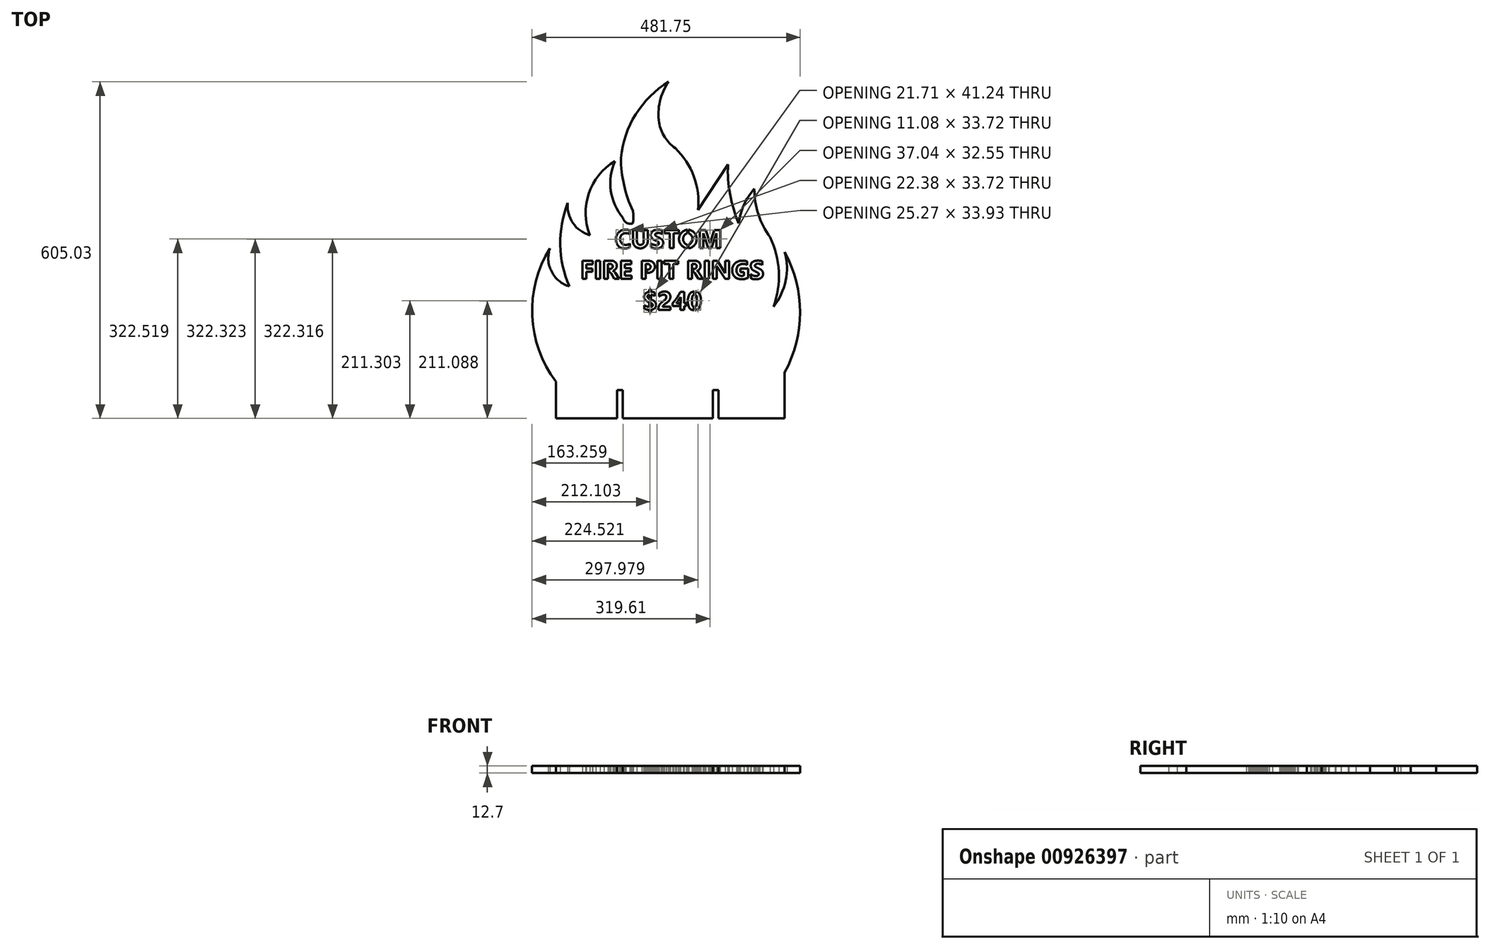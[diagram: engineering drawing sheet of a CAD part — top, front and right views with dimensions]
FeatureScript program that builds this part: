
annotation { "Feature Type Name" : "Feature", "Feature Type Description" : "" }
export const myFeature = defineFeature(function(context is Context, id is Id, definition is map)
    precondition{}
    {
        {
            var Q0;
            Q0=qCreatedBy(makeId("Top.planeOp"),FACE);
            var sketch = newSketch(context, id + "F0", { "sketchPlane" : qUnion([Q0])});
            skArc(sketch, "E0", {"start": v(108.84, 331.84) * mm, "mid": v(102.03, 332.98) * mm, "end": v(95.2, 331.92) * mm});
            skArc(sketch, "E1", {"start": v(95.2, 331.92) * mm, "mid": v(85.87, 324.34) * mm, "end": v(84.03, 312.45) * mm});
            skArc(sketch, "E2", {"start": v(84.03, 312.45) * mm, "mid": v(89.83, 302.02) * mm, "end": v(101.45, 299.3) * mm});
            skArc(sketch, "E3", {"start": v(101.45, 299.3) * mm, "mid": v(105.29, 299.76) * mm, "end": v(108.84, 301.28) * mm});
            skArc(sketch, "E4", {"start": v(96.85, 306.45) * mm, "mid": v(103.08, 305.63) * mm, "end": v(108.92, 307.93) * mm});
            skArc(sketch, "E5", {"start": v(91.34, 317.62) * mm, "mid": v(92.31, 311.16) * mm, "end": v(96.85, 306.45) * mm});
            skArc(sketch, "E6", {"start": v(98.74, 326.41) * mm, "mid": v(93.7, 323.14) * mm, "end": v(91.34, 317.62) * mm});
            skArc(sketch, "E7", {"start": v(108.84, 324.52) * mm, "mid": v(103.99, 326.53) * mm, "end": v(98.74, 326.41) * mm});
            skLineSegment(sketch, "E8", {"start": v(108.84, 331.84) * mm, "end": v(108.84, 324.52) * mm});
            skLineSegment(sketch, "E9", {"start": v(108.92, 307.93) * mm, "end": v(108.84, 301.28) * mm});
            skLineSegment(sketch, "E10", {"start": v(114.18, 332.5) * mm, "end": v(121.57, 332.5) * mm});
            skLineSegment(sketch, "E11", {"start": v(121.57, 332.5) * mm, "end": v(121.57, 311.55) * mm});
            skLineSegment(sketch, "E12", {"start": v(114.18, 332.5) * mm, "end": v(114.18, 311.22) * mm});
            skLineSegment(sketch, "E13", {"start": v(133.65, 332.5) * mm, "end": v(141.12, 332.5) * mm});
            skLineSegment(sketch, "E14", {"start": v(141.12, 332.5) * mm, "end": v(141.12, 311.63) * mm});
            skLineSegment(sketch, "E15", {"start": v(133.65, 332.5) * mm, "end": v(133.65, 311.63) * mm});
            skArc(sketch, "E16", {"start": v(121.57, 311.55) * mm, "mid": v(127.65, 305.59) * mm, "end": v(133.65, 311.63) * mm});
            skArc(sketch, "E17", {"start": v(114.18, 311.22) * mm, "mid": v(127.84, 299.32) * mm, "end": v(141.12, 311.63) * mm});
            skArc(sketch, "E18", {"start": v(167.33, 325.02) * mm, "mid": v(162.06, 326.88) * mm, "end": v(156.49, 326.41) * mm});
            skArc(sketch, "E19", {"start": v(156.49, 326.41) * mm, "mid": v(154.37, 324.68) * mm, "end": v(155.17, 322.06) * mm});
            skArc(sketch, "E20", {"start": v(155.17, 322.06) * mm, "mid": v(156.94, 320.64) * mm, "end": v(158.95, 319.6) * mm});
            skArc(sketch, "E21", {"start": v(166.43, 315.24) * mm, "mid": v(162.87, 317.73) * mm, "end": v(158.95, 319.6) * mm});
            skArc(sketch, "E22", {"start": v(168.07, 305.22) * mm, "mid": v(168.61, 310.45) * mm, "end": v(166.43, 315.24) * mm});
            skArc(sketch, "E23", {"start": v(159.77, 299.47) * mm, "mid": v(164.61, 301.34) * mm, "end": v(168.07, 305.22) * mm});
            skArc(sketch, "E24", {"start": v(146.63, 301.28) * mm, "mid": v(153.06, 299.37) * mm, "end": v(159.77, 299.47) * mm});
            skArc(sketch, "E25", {"start": v(146.55, 308.34) * mm, "mid": v(149.66, 306.42) * mm, "end": v(153.2, 305.47) * mm});
            skArc(sketch, "E26", {"start": v(153.2, 305.47) * mm, "mid": v(156.77, 305.1) * mm, "end": v(160.1, 306.45) * mm});
            skArc(sketch, "E27", {"start": v(160.1, 306.45) * mm, "mid": v(160.96, 308.28) * mm, "end": v(160.47, 310.23) * mm});
            skArc(sketch, "E28", {"start": v(160.47, 310.23) * mm, "mid": v(158.3, 312.04) * mm, "end": v(155.7, 313.15) * mm});
            skArc(sketch, "E29", {"start": v(148.35, 317.75) * mm, "mid": v(151.7, 314.9) * mm, "end": v(155.7, 313.15) * mm});
            skArc(sketch, "E30", {"start": v(146.83, 326.13) * mm, "mid": v(146.5, 321.74) * mm, "end": v(148.35, 317.75) * mm});
            skArc(sketch, "E31", {"start": v(154.6, 332.37) * mm, "mid": v(149.89, 330.28) * mm, "end": v(146.83, 326.13) * mm});
            skArc(sketch, "E32", {"start": v(167.17, 331.67) * mm, "mid": v(160.93, 332.85) * mm, "end": v(154.6, 332.37) * mm});
            skLineSegment(sketch, "E33", {"start": v(167.17, 331.67) * mm, "end": v(167.33, 325.02) * mm});
            skLineSegment(sketch, "E34", {"start": v(146.63, 301.28) * mm, "end": v(146.55, 308.34) * mm});
            skLineSegment(sketch, "E35", {"start": v(171.08, 332.5) * mm, "end": v(196.87, 332.5) * mm});
            skLineSegment(sketch, "E36", {"start": v(196.87, 332.5) * mm, "end": v(196.87, 326.44) * mm});
            skLineSegment(sketch, "E37", {"start": v(196.87, 326.44) * mm, "end": v(187.54, 326.44) * mm});
            skLineSegment(sketch, "E38", {"start": v(187.54, 326.44) * mm, "end": v(187.54, 299.95) * mm});
            skLineSegment(sketch, "E39", {"start": v(187.54, 299.95) * mm, "end": v(180.38, 299.95) * mm});
            skLineSegment(sketch, "E40", {"start": v(180.38, 299.95) * mm, "end": v(180.38, 326.44) * mm});
            skLineSegment(sketch, "E41", {"start": v(180.38, 326.44) * mm, "end": v(171.08, 326.44) * mm});
            skLineSegment(sketch, "E42", {"start": v(171.08, 326.44) * mm, "end": v(171.08, 332.5) * mm});
            skLineSegment(sketch, "E43", {"start": v(234.12, 332.5) * mm, "end": v(244.97, 332.5) * mm});
            skLineSegment(sketch, "E44", {"start": v(244.97, 332.5) * mm, "end": v(252.7, 308.44) * mm});
            skLineSegment(sketch, "E45", {"start": v(234.12, 332.5) * mm, "end": v(234.12, 299.95) * mm});
            skLineSegment(sketch, "E46", {"start": v(234.12, 299.95) * mm, "end": v(240.8, 299.95) * mm});
            skLineSegment(sketch, "E47", {"start": v(240.8, 299.95) * mm, "end": v(240.5, 326.23) * mm});
            skLineSegment(sketch, "E48", {"start": v(240.5, 326.23) * mm, "end": v(249.5, 299.95) * mm});
            skLineSegment(sketch, "E49", {"start": v(249.5, 299.95) * mm, "end": v(255.46, 299.95) * mm});
            skLineSegment(sketch, "E50", {"start": v(255.46, 299.95) * mm, "end": v(264.18, 326.2) * mm});
            skLineSegment(sketch, "E51", {"start": v(264.18, 326.2) * mm, "end": v(264.18, 299.95) * mm});
            skLineSegment(sketch, "E52", {"start": v(264.18, 299.95) * mm, "end": v(271.16, 299.95) * mm});
            skLineSegment(sketch, "E53", {"start": v(271.16, 299.95) * mm, "end": v(271.16, 332.5) * mm});
            skLineSegment(sketch, "E54", {"start": v(271.16, 332.5) * mm, "end": v(260.73, 332.44) * mm});
            skLineSegment(sketch, "E55", {"start": v(260.73, 332.44) * mm, "end": v(252.7, 308.44) * mm});
            skLineSegment(sketch, "E56", {"start": v(212.35, 305.64) * mm, "end": v(212.35, 299.43) * mm});
            skLineSegment(sketch, "E57", {"start": v(214.07, 299.34) * mm, "end": v(214.07, 305.67) * mm});
            skLineSegment(sketch, "E58", {"start": v(212.24, 332.8) * mm, "end": v(212.24, 326.62) * mm});
            skLineSegment(sketch, "E59", {"start": v(213.94, 326.58) * mm, "end": v(213.94, 332.78) * mm});
            skArc(sketch, "E60", {"start": v(212.24, 332.8) * mm, "mid": v(197.08, 316.07) * mm, "end": v(212.35, 299.43) * mm});
            skArc(sketch, "E61", {"start": v(214.07, 299.34) * mm, "mid": v(228.95, 316.12) * mm, "end": v(213.94, 332.78) * mm});
            skArc(sketch, "E62", {"start": v(212.24, 326.62) * mm, "mid": v(204.51, 316.1) * mm, "end": v(212.35, 305.64) * mm});
            skArc(sketch, "E63", {"start": v(214.07, 305.67) * mm, "mid": v(221.3, 316.17) * mm, "end": v(213.94, 326.58) * mm});
            skLineSegment(sketch, "E64", {"start": v(23.38, 277.03) * mm, "end": v(42.19, 277.03) * mm});
            skLineSegment(sketch, "E65", {"start": v(42.19, 277.03) * mm, "end": v(42.19, 270.93) * mm});
            skLineSegment(sketch, "E66", {"start": v(42.19, 270.93) * mm, "end": v(30.72, 270.93) * mm});
            skLineSegment(sketch, "E67", {"start": v(30.72, 270.93) * mm, "end": v(30.72, 262.92) * mm});
            skLineSegment(sketch, "E68", {"start": v(30.72, 262.92) * mm, "end": v(41.2, 262.92) * mm});
            skLineSegment(sketch, "E69", {"start": v(41.2, 262.92) * mm, "end": v(41.2, 257.13) * mm});
            skLineSegment(sketch, "E70", {"start": v(41.2, 257.13) * mm, "end": v(30.74, 257.13) * mm});
            skLineSegment(sketch, "E71", {"start": v(30.74, 257.13) * mm, "end": v(30.74, 244.43) * mm});
            skLineSegment(sketch, "E72", {"start": v(30.74, 244.43) * mm, "end": v(23.38, 244.43) * mm});
            skLineSegment(sketch, "E73", {"start": v(23.38, 244.43) * mm, "end": v(23.38, 277.03) * mm});
            skLineSegment(sketch, "E74.bottom", {"start": v(47.55, 277.03) * mm, "end": v(55.04, 277.03) * mm});
            skLineSegment(sketch, "E74.top", {"start": v(47.55, 244.43) * mm, "end": v(55.04, 244.43) * mm});
            skLineSegment(sketch, "E74.left", {"start": v(47.55, 277.03) * mm, "end": v(47.55, 244.43) * mm});
            skLineSegment(sketch, "E74.right", {"start": v(55.04, 277.03) * mm, "end": v(55.04, 244.43) * mm});
            skLineSegment(sketch, "E75", {"start": v(62.3, 244.43) * mm, "end": v(62.3, 277.03) * mm});
            skLineSegment(sketch, "E76", {"start": v(62.3, 277.03) * mm, "end": v(76.13, 277.03) * mm});
            skLineSegment(sketch, "E77", {"start": v(62.3, 244.43) * mm, "end": v(69.5, 244.43) * mm});
            skLineSegment(sketch, "E78", {"start": v(69.5, 244.43) * mm, "end": v(69.5, 271.2) * mm});
            skLineSegment(sketch, "E79", {"start": v(69.5, 271.2) * mm, "end": v(74.39, 271.2) * mm});
            skLineSegment(sketch, "E80", {"start": v(71.2, 262.43) * mm, "end": v(73.51, 262.43) * mm});
            skLineSegment(sketch, "E81", {"start": v(71.2, 262.43) * mm, "end": v(71.2, 256.8) * mm});
            skLineSegment(sketch, "E82", {"start": v(71.2, 256.8) * mm, "end": v(71.77, 256.8) * mm});
            skLineSegment(sketch, "E83", {"start": v(74.9, 254.53) * mm, "end": v(80.9, 244.43) * mm});
            skLineSegment(sketch, "E84", {"start": v(80.9, 244.43) * mm, "end": v(89.31, 244.43) * mm});
            skLineSegment(sketch, "E85", {"start": v(89.31, 244.43) * mm, "end": v(82.46, 255.51) * mm});
            skArc(sketch, "E86", {"start": v(73.51, 262.43) * mm, "mid": v(77.92, 266.42) * mm, "end": v(74.39, 271.2) * mm});
            skArc(sketch, "E87", {"start": v(74.9, 254.53) * mm, "mid": v(73.58, 255.98) * mm, "end": v(71.77, 256.8) * mm});
            skArc(sketch, "E88", {"start": v(82.46, 255.51) * mm, "mid": v(80.72, 257.54) * mm, "end": v(78.44, 258.93) * mm});
            skArc(sketch, "E89", {"start": v(78.44, 258.93) * mm, "mid": v(85.25, 269) * mm, "end": v(76.13, 277.03) * mm});
            skLineSegment(sketch, "E90", {"start": v(92.56, 244.46) * mm, "end": v(92.56, 276.9) * mm});
            skLineSegment(sketch, "E91", {"start": v(92.56, 276.9) * mm, "end": v(111.32, 276.9) * mm});
            skLineSegment(sketch, "E92", {"start": v(111.32, 276.9) * mm, "end": v(111.32, 270.93) * mm});
            skLineSegment(sketch, "E93", {"start": v(111.32, 270.93) * mm, "end": v(99.9, 270.93) * mm});
            skLineSegment(sketch, "E94", {"start": v(99.9, 270.93) * mm, "end": v(99.9, 263.66) * mm});
            skLineSegment(sketch, "E95", {"start": v(99.9, 263.66) * mm, "end": v(110.4, 263.66) * mm});
            skLineSegment(sketch, "E96", {"start": v(110.4, 263.66) * mm, "end": v(110.4, 257.75) * mm});
            skLineSegment(sketch, "E97", {"start": v(110.4, 257.75) * mm, "end": v(99.9, 257.75) * mm});
            skLineSegment(sketch, "E98", {"start": v(99.9, 257.75) * mm, "end": v(99.9, 250.42) * mm});
            skLineSegment(sketch, "E99", {"start": v(99.9, 250.42) * mm, "end": v(111.86, 250.42) * mm});
            skLineSegment(sketch, "E100", {"start": v(111.86, 250.42) * mm, "end": v(111.86, 244.36) * mm});
            skLineSegment(sketch, "E101", {"start": v(111.86, 244.36) * mm, "end": v(92.56, 244.46) * mm});
            skLineSegment(sketch, "E102", {"start": v(130.03, 244.46) * mm, "end": v(130.03, 276.82) * mm});
            skLineSegment(sketch, "E103", {"start": v(130.03, 276.82) * mm, "end": v(143.4, 276.82) * mm});
            skLineSegment(sketch, "E104", {"start": v(130.03, 244.46) * mm, "end": v(137.35, 244.46) * mm});
            skLineSegment(sketch, "E105", {"start": v(137.35, 244.46) * mm, "end": v(137.35, 271.2) * mm});
            skLineSegment(sketch, "E106", {"start": v(137.35, 271.2) * mm, "end": v(141.55, 271.2) * mm});
            skLineSegment(sketch, "E107", {"start": v(138.92, 255.57) * mm, "end": v(138.92, 261.1) * mm});
            skLineSegment(sketch, "E108", {"start": v(138.92, 261.1) * mm, "end": v(140.87, 261.1) * mm});
            skArc(sketch, "E109", {"start": v(140.87, 261.1) * mm, "mid": v(145.94, 265.83) * mm, "end": v(141.55, 271.2) * mm});
            skArc(sketch, "E110", {"start": v(153.42, 264.02) * mm, "mid": v(151.53, 272.86) * mm, "end": v(143.4, 276.82) * mm});
            skArc(sketch, "E111", {"start": v(138.92, 255.57) * mm, "mid": v(147.84, 256.93) * mm, "end": v(153.42, 264.02) * mm});
            skLineSegment(sketch, "E112.bottom", {"start": v(158.46, 276.94) * mm, "end": v(165.74, 276.94) * mm});
            skLineSegment(sketch, "E112.top", {"start": v(158.46, 244.46) * mm, "end": v(165.74, 244.46) * mm});
            skLineSegment(sketch, "E112.left", {"start": v(158.46, 276.94) * mm, "end": v(158.46, 244.46) * mm});
            skLineSegment(sketch, "E112.right", {"start": v(165.74, 276.94) * mm, "end": v(165.74, 244.46) * mm});
            skLineSegment(sketch, "E113", {"start": v(170.03, 271) * mm, "end": v(170.03, 276.94) * mm});
            skLineSegment(sketch, "E114", {"start": v(170.03, 276.94) * mm, "end": v(195.82, 276.94) * mm});
            skLineSegment(sketch, "E115", {"start": v(195.82, 276.94) * mm, "end": v(195.82, 271.08) * mm});
            skLineSegment(sketch, "E116", {"start": v(195.82, 271.08) * mm, "end": v(186.62, 271.08) * mm});
            skLineSegment(sketch, "E117", {"start": v(186.62, 271.08) * mm, "end": v(186.62, 244.63) * mm});
            skLineSegment(sketch, "E118", {"start": v(186.62, 244.63) * mm, "end": v(179.48, 244.63) * mm});
            skLineSegment(sketch, "E119", {"start": v(179.48, 244.63) * mm, "end": v(179.48, 271.08) * mm});
            skLineSegment(sketch, "E120", {"start": v(179.48, 271.08) * mm, "end": v(170.03, 271) * mm});
            skLineSegment(sketch, "E121", {"start": v(213.11, 244.5) * mm, "end": v(213.11, 276.94) * mm});
            skLineSegment(sketch, "E122", {"start": v(213.11, 276.94) * mm, "end": v(226.58, 276.94) * mm});
            skLineSegment(sketch, "E123", {"start": v(213.11, 244.5) * mm, "end": v(220.5, 244.5) * mm});
            skLineSegment(sketch, "E124", {"start": v(220.5, 244.5) * mm, "end": v(220.5, 271.44) * mm});
            skLineSegment(sketch, "E125", {"start": v(220.5, 271.44) * mm, "end": v(224.92, 271.44) * mm});
            skLineSegment(sketch, "E126", {"start": v(222.09, 262.42) * mm, "end": v(222.09, 256.9) * mm});
            skLineSegment(sketch, "E127", {"start": v(222.09, 256.9) * mm, "end": v(222.93, 256.9) * mm});
            skLineSegment(sketch, "E128", {"start": v(222.09, 262.42) * mm, "end": v(224.2, 262.42) * mm});
            skLineSegment(sketch, "E129", {"start": v(225.52, 254.75) * mm, "end": v(231.88, 244.5) * mm});
            skLineSegment(sketch, "E130", {"start": v(231.88, 244.5) * mm, "end": v(240.27, 244.5) * mm});
            skLineSegment(sketch, "E131", {"start": v(240.27, 244.5) * mm, "end": v(232.78, 256.12) * mm});
            skArc(sketch, "E132", {"start": v(225.52, 254.75) * mm, "mid": v(224.48, 256) * mm, "end": v(223.13, 256.9) * mm});
            skArc(sketch, "E133", {"start": v(232.78, 256.12) * mm, "mid": v(231.29, 257.76) * mm, "end": v(229.35, 258.85) * mm});
            skArc(sketch, "E134", {"start": v(229.35, 258.85) * mm, "mid": v(235.73, 269.08) * mm, "end": v(226.58, 276.94) * mm});
            skArc(sketch, "E135", {"start": v(224.2, 262.42) * mm, "mid": v(228.73, 266.6) * mm, "end": v(224.92, 271.44) * mm});
            skLineSegment(sketch, "E136.bottom", {"start": v(243.31, 276.94) * mm, "end": v(250.8, 276.94) * mm});
            skLineSegment(sketch, "E136.top", {"start": v(243.31, 244.42) * mm, "end": v(250.8, 244.42) * mm});
            skLineSegment(sketch, "E136.left", {"start": v(243.31, 276.94) * mm, "end": v(243.31, 244.42) * mm});
            skLineSegment(sketch, "E136.right", {"start": v(250.8, 276.94) * mm, "end": v(250.8, 244.42) * mm});
            skLineSegment(sketch, "E137", {"start": v(258.1, 244.42) * mm, "end": v(258.1, 276.94) * mm});
            skLineSegment(sketch, "E138", {"start": v(258.1, 276.94) * mm, "end": v(265.96, 276.94) * mm});
            skLineSegment(sketch, "E139", {"start": v(265.96, 276.94) * mm, "end": v(280.37, 254.52) * mm});
            skLineSegment(sketch, "E140", {"start": v(280.37, 254.52) * mm, "end": v(280.37, 276.94) * mm});
            skLineSegment(sketch, "E141", {"start": v(280.37, 276.94) * mm, "end": v(287.16, 276.94) * mm});
            skLineSegment(sketch, "E142", {"start": v(287.16, 276.94) * mm, "end": v(287.21, 244.46) * mm});
            skLineSegment(sketch, "E143", {"start": v(287.21, 244.46) * mm, "end": v(279.88, 244.36) * mm});
            skLineSegment(sketch, "E144", {"start": v(279.88, 244.36) * mm, "end": v(264.84, 267.42) * mm});
            skLineSegment(sketch, "E145", {"start": v(264.84, 267.42) * mm, "end": v(264.84, 244.42) * mm});
            skLineSegment(sketch, "E146", {"start": v(264.84, 244.42) * mm, "end": v(258.1, 244.42) * mm});
            skLineSegment(sketch, "E147", {"start": v(319.74, 275.95) * mm, "end": v(319.74, 269.15) * mm});
            skLineSegment(sketch, "E148", {"start": v(314, 250.8) * mm, "end": v(314, 256.96) * mm});
            skLineSegment(sketch, "E149", {"start": v(314, 256.96) * mm, "end": v(307.43, 256.96) * mm});
            skLineSegment(sketch, "E150", {"start": v(307.43, 256.96) * mm, "end": v(307.43, 262.88) * mm});
            skLineSegment(sketch, "E151", {"start": v(307.43, 262.88) * mm, "end": v(321.25, 262.88) * mm});
            skLineSegment(sketch, "E152", {"start": v(321.25, 262.88) * mm, "end": v(321.25, 246.67) * mm});
            skArc(sketch, "E153", {"start": v(319.74, 269.15) * mm, "mid": v(311.3, 271.47) * mm, "end": v(303.19, 268.17) * mm});
            skArc(sketch, "E154", {"start": v(303.19, 268.17) * mm, "mid": v(300.3, 260.38) * mm, "end": v(303.19, 252.6) * mm});
            skArc(sketch, "E155", {"start": v(303.19, 252.6) * mm, "mid": v(308.3, 249.93) * mm, "end": v(314, 250.8) * mm});
            skArc(sketch, "E156", {"start": v(319.74, 275.95) * mm, "mid": v(310.68, 277.26) * mm, "end": v(301.74, 275.31) * mm});
            skArc(sketch, "E157", {"start": v(301.74, 275.31) * mm, "mid": v(294.33, 267.76) * mm, "end": v(292.79, 257.3) * mm});
            skArc(sketch, "E158", {"start": v(292.79, 257.3) * mm, "mid": v(296.71, 248.76) * mm, "end": v(304.99, 244.3) * mm});
            skArc(sketch, "E159", {"start": v(304.99, 244.3) * mm, "mid": v(313.34, 243.96) * mm, "end": v(321.25, 246.67) * mm});
            skArc(sketch, "E160", {"start": v(326.05, 252.95) * mm, "mid": v(330.49, 250.43) * mm, "end": v(335.54, 249.7) * mm});
            skArc(sketch, "E161", {"start": v(335.54, 249.7) * mm, "mid": v(338.07, 250) * mm, "end": v(340.07, 251.57) * mm});
            skArc(sketch, "E162", {"start": v(340.07, 251.57) * mm, "mid": v(340.28, 253.95) * mm, "end": v(338.62, 255.68) * mm});
            skArc(sketch, "E163", {"start": v(331.3, 259.44) * mm, "mid": v(334.93, 257.5) * mm, "end": v(338.62, 255.68) * mm});
            skArc(sketch, "E164", {"start": v(326.15, 266.04) * mm, "mid": v(327.94, 262.13) * mm, "end": v(331.3, 259.44) * mm});
            skArc(sketch, "E165", {"start": v(331.95, 276.26) * mm, "mid": v(327.09, 272.27) * mm, "end": v(326.15, 266.04) * mm});
            skArc(sketch, "E166", {"start": v(346.74, 276.26) * mm, "mid": v(339.34, 277.34) * mm, "end": v(331.95, 276.26) * mm});
            skArc(sketch, "E167", {"start": v(346.8, 269.43) * mm, "mid": v(342.9, 271.2) * mm, "end": v(338.62, 271.53) * mm});
            skArc(sketch, "E168", {"start": v(338.62, 271.53) * mm, "mid": v(336.04, 271.19) * mm, "end": v(334.02, 269.53) * mm});
            skArc(sketch, "E169", {"start": v(334.02, 269.53) * mm, "mid": v(333.75, 267.57) * mm, "end": v(335, 266.04) * mm});
            skArc(sketch, "E170", {"start": v(335, 266.04) * mm, "mid": v(338.47, 264.04) * mm, "end": v(342.1, 262.35) * mm});
            skArc(sketch, "E171", {"start": v(347.88, 256.2) * mm, "mid": v(345.68, 259.92) * mm, "end": v(342.1, 262.35) * mm});
            skArc(sketch, "E172", {"start": v(346.77, 248.22) * mm, "mid": v(348.04, 252.1) * mm, "end": v(347.88, 256.2) * mm});
            skArc(sketch, "E173", {"start": v(339.32, 244) * mm, "mid": v(343.39, 245.51) * mm, "end": v(346.77, 248.22) * mm});
            skArc(sketch, "E174", {"start": v(326.15, 245.56) * mm, "mid": v(328.4, 244.63) * mm, "end": v(330.76, 244.05) * mm});
            skLineSegment(sketch, "E175", {"start": v(326.05, 252.95) * mm, "end": v(326.15, 245.56) * mm});
            skLineSegment(sketch, "E176", {"start": v(346.74, 276.26) * mm, "end": v(346.8, 269.43) * mm});
            skArc(sketch, "E177", {"start": v(330.76, 244.05) * mm, "mid": v(335.04, 243.7) * mm, "end": v(339.32, 244) * mm});
            skLineSegment(sketch, "E178", {"start": v(143.42, 225.4) * mm, "end": v(146.63, 225.4) * mm});
            skLineSegment(sketch, "E179", {"start": v(146.63, 225.4) * mm, "end": v(146.63, 221.26) * mm});
            skLineSegment(sketch, "E180", {"start": v(143.42, 225.4) * mm, "end": v(143.42, 221.23) * mm});
            skLineSegment(sketch, "E181", {"start": v(143.39, 215.84) * mm, "end": v(143.39, 210.14) * mm});
            skLineSegment(sketch, "E182", {"start": v(143.39, 210.14) * mm, "end": v(146.67, 208.76) * mm});
            skLineSegment(sketch, "E183", {"start": v(146.67, 208.76) * mm, "end": v(146.67, 215.9) * mm});
            skArc(sketch, "E184", {"start": v(153.75, 219.74) * mm, "mid": v(150.29, 220.94) * mm, "end": v(146.63, 221.26) * mm});
            skArc(sketch, "E185", {"start": v(153.75, 213.7) * mm, "mid": v(150.33, 215.18) * mm, "end": v(146.67, 215.9) * mm});
            skArc(sketch, "E186", {"start": v(143.42, 221.23) * mm, "mid": v(138.89, 219.79) * mm, "end": v(135.48, 216.46) * mm});
            skArc(sketch, "E187", {"start": v(135.48, 216.46) * mm, "mid": v(134.34, 211.01) * mm, "end": v(136.82, 206.03) * mm});
            skArc(sketch, "E188", {"start": v(143.39, 215.84) * mm, "mid": v(140.98, 214.73) * mm, "end": v(140.38, 212.14) * mm});
            skArc(sketch, "E189", {"start": v(140.38, 212.14) * mm, "mid": v(141.48, 210.02) * mm, "end": v(143.42, 208.62) * mm});
            skArc(sketch, "E190", {"start": v(155.93, 198.47) * mm, "mid": v(154.07, 203.14) * mm, "end": v(149.98, 206.07) * mm});
            skArc(sketch, "E191", {"start": v(152.2, 190.7) * mm, "mid": v(155.21, 194.03) * mm, "end": v(155.93, 198.47) * mm});
            skArc(sketch, "E192", {"start": v(146.67, 188.9) * mm, "mid": v(149.55, 189.42) * mm, "end": v(152.2, 190.7) * mm});
            skArc(sketch, "E193", {"start": v(146.67, 194.22) * mm, "mid": v(148.96, 195.05) * mm, "end": v(149.92, 197.3) * mm});
            skArc(sketch, "E194", {"start": v(149.92, 197.3) * mm, "mid": v(148.94, 199.47) * mm, "end": v(147.01, 200.89) * mm});
            skArc(sketch, "E195", {"start": v(136.82, 206.03) * mm, "mid": v(139.24, 204.31) * mm, "end": v(141.9, 203.03) * mm});
            skLineSegment(sketch, "E196", {"start": v(143.42, 208.62) * mm, "end": v(149.98, 206.07) * mm});
            skLineSegment(sketch, "E197", {"start": v(147.01, 200.89) * mm, "end": v(141.9, 203.03) * mm});
            skLineSegment(sketch, "E198", {"start": v(146.67, 194.22) * mm, "end": v(146.67, 199.64) * mm});
            skLineSegment(sketch, "E199", {"start": v(146.67, 199.64) * mm, "end": v(143.42, 201) * mm});
            skLineSegment(sketch, "E200", {"start": v(143.42, 201) * mm, "end": v(143.42, 194.08) * mm});
            skArc(sketch, "E201", {"start": v(134.9, 197.09) * mm, "mid": v(138.95, 194.99) * mm, "end": v(143.42, 194.08) * mm});
            skLineSegment(sketch, "E202", {"start": v(134.9, 197.09) * mm, "end": v(134.9, 190.82) * mm});
            skArc(sketch, "E203", {"start": v(134.9, 190.82) * mm, "mid": v(139.02, 189.26) * mm, "end": v(143.4, 188.81) * mm});
            skLineSegment(sketch, "E204", {"start": v(143.4, 188.81) * mm, "end": v(143.4, 184.17) * mm});
            skLineSegment(sketch, "E205", {"start": v(143.4, 184.17) * mm, "end": v(146.67, 184.17) * mm});
            skLineSegment(sketch, "E206", {"start": v(146.67, 184.17) * mm, "end": v(146.67, 188.9) * mm});
            skLineSegment(sketch, "E207", {"start": v(153.75, 219.74) * mm, "end": v(153.75, 213.7) * mm});
            skLineSegment(sketch, "E208", {"start": v(161.6, 212.73) * mm, "end": v(161.6, 218.93) * mm});
            skArc(sketch, "E209", {"start": v(174.38, 221.48) * mm, "mid": v(167.76, 221.38) * mm, "end": v(161.6, 218.93) * mm});
            skArc(sketch, "E210", {"start": v(181.45, 214.13) * mm, "mid": v(179.03, 218.88) * mm, "end": v(174.38, 221.48) * mm});
            skArc(sketch, "E211", {"start": v(177.83, 203.82) * mm, "mid": v(180.88, 208.54) * mm, "end": v(181.45, 214.13) * mm});
            skArc(sketch, "E212", {"start": v(177.83, 203.82) * mm, "mid": v(173.98, 200.9) * mm, "end": v(170.15, 197.94) * mm});
            skArc(sketch, "E213", {"start": v(170.15, 197.94) * mm, "mid": v(168.78, 196.5) * mm, "end": v(167.93, 194.7) * mm});
            skLineSegment(sketch, "E214", {"start": v(167.93, 194.7) * mm, "end": v(181.53, 194.7) * mm});
            skLineSegment(sketch, "E215", {"start": v(181.53, 194.7) * mm, "end": v(181.53, 188.83) * mm});
            skLineSegment(sketch, "E216", {"start": v(181.53, 188.83) * mm, "end": v(160.09, 188.83) * mm});
            skLineSegment(sketch, "E217", {"start": v(160.09, 188.83) * mm, "end": v(160.09, 192.69) * mm});
            skArc(sketch, "E218", {"start": v(164.32, 200.86) * mm, "mid": v(161.57, 197.1) * mm, "end": v(160.09, 192.69) * mm});
            skArc(sketch, "E219", {"start": v(171.14, 206.16) * mm, "mid": v(167.66, 203.6) * mm, "end": v(164.32, 200.86) * mm});
            skArc(sketch, "E220", {"start": v(171.14, 206.16) * mm, "mid": v(173.35, 208.78) * mm, "end": v(174.34, 212.07) * mm});
            skArc(sketch, "E221", {"start": v(174.34, 212.07) * mm, "mid": v(173.44, 214.56) * mm, "end": v(171.14, 215.85) * mm});
            skArc(sketch, "E222", {"start": v(171.14, 215.85) * mm, "mid": v(168.3, 215.88) * mm, "end": v(165.55, 215.11) * mm});
            skArc(sketch, "E223", {"start": v(165.55, 215.11) * mm, "mid": v(163.44, 214.16) * mm, "end": v(161.6, 212.73) * mm});
            skArc(sketch, "E224", {"start": v(185.72, 200.86) * mm, "mid": v(193.36, 210.57) * mm, "end": v(199.6, 221.23) * mm});
            skArc(sketch, "E225", {"start": v(192.17, 200.86) * mm, "mid": v(196.2, 206.2) * mm, "end": v(199.8, 211.84) * mm});
            skLineSegment(sketch, "E226", {"start": v(199.6, 221.23) * mm, "end": v(206.32, 221.23) * mm});
            skLineSegment(sketch, "E227", {"start": v(206.32, 221.23) * mm, "end": v(206.32, 200.82) * mm});
            skLineSegment(sketch, "E228", {"start": v(206.32, 200.82) * mm, "end": v(210.08, 200.82) * mm});
            skLineSegment(sketch, "E229", {"start": v(210.08, 200.82) * mm, "end": v(210.08, 195.45) * mm});
            skLineSegment(sketch, "E230", {"start": v(210.08, 195.45) * mm, "end": v(206.32, 195.45) * mm});
            skLineSegment(sketch, "E231", {"start": v(206.32, 195.45) * mm, "end": v(206.32, 188.75) * mm});
            skLineSegment(sketch, "E232", {"start": v(206.32, 188.75) * mm, "end": v(199.6, 188.75) * mm});
            skLineSegment(sketch, "E233", {"start": v(199.6, 188.75) * mm, "end": v(199.8, 211.84) * mm});
            skLineSegment(sketch, "E234", {"start": v(192.17, 200.86) * mm, "end": v(198.06, 200.86) * mm});
            skLineSegment(sketch, "E235", {"start": v(198.06, 200.86) * mm, "end": v(198.06, 195.5) * mm});
            skLineSegment(sketch, "E236", {"start": v(198.06, 195.5) * mm, "end": v(185.72, 195.5) * mm});
            skLineSegment(sketch, "E237", {"start": v(185.72, 195.5) * mm, "end": v(185.72, 200.86) * mm});
            skArc(sketch, "E238", {"start": v(224.15, 221.77) * mm, "mid": v(218.17, 219.34) * mm, "end": v(214.52, 214) * mm});
            skArc(sketch, "E239", {"start": v(214.52, 214) * mm, "mid": v(212.87, 204.34) * mm, "end": v(214.52, 194.66) * mm});
            skArc(sketch, "E240", {"start": v(214.52, 194.66) * mm, "mid": v(218.14, 189.97) * mm, "end": v(223.8, 188.22) * mm});
            skArc(sketch, "E241", {"start": v(220.53, 199.72) * mm, "mid": v(221.36, 196.32) * mm, "end": v(223.8, 193.8) * mm});
            skArc(sketch, "E242", {"start": v(224.24, 216.2) * mm, "mid": v(221.9, 214.49) * mm, "end": v(220.91, 211.76) * mm});
            skArc(sketch, "E243", {"start": v(220.91, 211.76) * mm, "mid": v(220.21, 205.76) * mm, "end": v(220.53, 199.72) * mm});
            skArc(sketch, "E244", {"start": v(228.55, 212.21) * mm, "mid": v(227.69, 214.48) * mm, "end": v(225.92, 216.15) * mm});
            skArc(sketch, "E245", {"start": v(225.47, 193.69) * mm, "mid": v(227.35, 194.95) * mm, "end": v(228.3, 197.01) * mm});
            skArc(sketch, "E246", {"start": v(228.3, 197.01) * mm, "mid": v(229.3, 204.6) * mm, "end": v(228.55, 212.21) * mm});
            skArc(sketch, "E247", {"start": v(235.16, 214.55) * mm, "mid": v(231.73, 219.74) * mm, "end": v(225.88, 221.86) * mm});
            skArc(sketch, "E248", {"start": v(225.55, 188.14) * mm, "mid": v(231.76, 190.82) * mm, "end": v(235.33, 196.56) * mm});
            skArc(sketch, "E249", {"start": v(235.33, 196.56) * mm, "mid": v(236.55, 205.57) * mm, "end": v(235.16, 214.55) * mm});
            skLineSegment(sketch, "E250", {"start": v(223.8, 193.8) * mm, "end": v(223.8, 188.22) * mm});
            skLineSegment(sketch, "E251", {"start": v(225.47, 193.69) * mm, "end": v(225.55, 188.14) * mm});
            skLineSegment(sketch, "E252", {"start": v(224.15, 221.77) * mm, "end": v(224.24, 216.2) * mm});
            skLineSegment(sketch, "E253", {"start": v(225.88, 221.86) * mm, "end": v(225.92, 216.15) * mm});
            skLineSegment(sketch, "E254", {"start": v(222.93, 256.9) * mm, "end": v(223.13, 256.9) * mm});
            skPoint(sketch, "E255", {"position": v(184.35, 69.87) * mm});
            skPoint(sketch, "E256", {"position": v(189.04, 599.76) * mm});
            skPoint(sketch, "E257", {"position": v(-20.41, 244.94) * mm});
            skPoint(sketch, "E258", {"position": v(398.49, 249.63) * mm});
            skArc(sketch, "E259", {"start": v(178.31, 598.73) * mm, "mid": v(119.29, 540.33) * mm, "end": v(92.66, 461.68) * mm});
            skArc(sketch, "E260", {"start": v(178.31, 598.73) * mm, "mid": v(162.71, 563.62) * mm, "end": v(161.18, 525.23) * mm});
            skArc(sketch, "E261", {"start": v(161.18, 525.23) * mm, "mid": v(171.47, 499.51) * mm, "end": v(190.47, 479.36) * mm});
            skArc(sketch, "E262", {"start": v(231.37, 368.28) * mm, "mid": v(223.8, 428.56) * mm, "end": v(190.47, 479.36) * mm});
            skArc(sketch, "E263", {"start": v(92.66, 461.68) * mm, "mid": v(98.26, 412.98) * mm, "end": v(114.2, 366.62) * mm});
            skArc(sketch, "E264", {"start": v(82.16, 456.15) * mm, "mid": v(74.55, 402.95) * mm, "end": v(96.53, 353.91) * mm});
            skArc(sketch, "E265", {"start": v(114.2, 344.52) * mm, "mid": v(115.29, 355.57) * mm, "end": v(114.2, 366.62) * mm});
            skArc(sketch, "E266", {"start": v(96.53, 353.91) * mm, "mid": v(103.19, 345.12) * mm, "end": v(114.2, 344.52) * mm});
            skArc(sketch, "E267", {"start": v(82.16, 456.15) * mm, "mid": v(34.89, 397.96) * mm, "end": v(36.84, 323.02) * mm});
            skArc(sketch, "E268", {"start": v(-2.95, 381) * mm, "mid": v(6.5, 344.84) * mm, "end": v(36.84, 323.02) * mm});
            skArc(sketch, "E269", {"start": v(-2.95, 381) * mm, "mid": v(-16.28, 305.71) * mm, "end": v(0, 231) * mm});
            skArc(sketch, "E270", {"start": v(-35, 299.26) * mm, "mid": v(-31.98, 257.7) * mm, "end": v(0, 231) * mm});
            skArc(sketch, "E271", {"start": v(-35, 299.26) * mm, "mid": v(-66.75, 177.8) * mm, "end": v(-24.22, 59.7) * mm});
            skArc(sketch, "E272", {"start": v(285.15, 450.66) * mm, "mid": v(288.7, 396.47) * mm, "end": v(304.54, 344.52) * mm});
            skArc(sketch, "E273", {"start": v(332.47, 406.3) * mm, "mid": v(313.65, 377.6) * mm, "end": v(304.54, 344.52) * mm});
            skArc(sketch, "E274", {"start": v(332.47, 406.3) * mm, "mid": v(339.62, 360.5) * mm, "end": v(360.73, 319.22) * mm});
            skArc(sketch, "E275", {"start": v(366.97, 194.68) * mm, "mid": v(376.5, 257.58) * mm, "end": v(360.73, 319.22) * mm});
            skArc(sketch, "E276", {"start": v(366.97, 194.68) * mm, "mid": v(388.8, 241.22) * mm, "end": v(387.02, 292.6) * mm});
            skArc(sketch, "E277", {"start": v(387.02, 76.38) * mm, "mid": v(414.78, 184.5) * mm, "end": v(387.02, 292.6) * mm});
            skLineSegment(sketch, "E278", {"start": v(231.37, 368.28) * mm, "end": v(285.15, 450.66) * mm});
            skLineSegment(sketch, "E279", {"start": v(-24.22, 59.7) * mm, "end": v(-24.22, -6.3) * mm});
            skLineSegment(sketch, "E280", {"start": v(-24.22, -6.3) * mm, "end": v(387.02, -6.3) * mm});
            skLineSegment(sketch, "E281", {"start": v(387.02, -6.3) * mm, "end": v(387.02, 76.38) * mm});
            skLineSegment(sketch, "E282.bottom", {"start": v(86.1, -6.3) * mm, "end": v(96, -6.3) * mm});
            skLineSegment(sketch, "E282.top", {"start": v(86.1, 44.5) * mm, "end": v(96, 44.5) * mm});
            skLineSegment(sketch, "E282.left", {"start": v(86.1, -6.3) * mm, "end": v(86.1, 44.5) * mm});
            skLineSegment(sketch, "E282.right", {"start": v(96, -6.3) * mm, "end": v(96, 44.5) * mm});
            skLineSegment(sketch, "E283.bottom", {"start": v(257.95, -6.3) * mm, "end": v(267.85, -6.3) * mm});
            skLineSegment(sketch, "E283.top", {"start": v(257.95, 44.5) * mm, "end": v(267.85, 44.5) * mm});
            skLineSegment(sketch, "E283.left", {"start": v(257.95, -6.3) * mm, "end": v(257.95, 44.5) * mm});
            skLineSegment(sketch, "E283.right", {"start": v(267.85, -6.3) * mm, "end": v(267.85, 44.5) * mm});
            skSolve(sketch);
        }
        {
            var Q0;
            Q0=makeQuery(id+"F0.imprint","IMPRINT",FACE,{"disambiguationData":[TD([[makeQuery(id+"F0.imprint","IMPRINT",EDGE,{"derivedFrom":sQuery(id+"F0.wireOp",EDGE,"E0")}),-1.0]])]});
            extrude(context, id + "F1", {"entities" : qUnion([Q0]), "depth" : 12.7 * mm, "offsetDistance" : 25.4 * mm});
        }
    });
